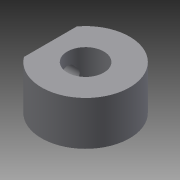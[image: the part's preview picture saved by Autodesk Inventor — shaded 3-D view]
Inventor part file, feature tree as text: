
AUTODESK INVENTOR PART (.ipt)
format: ipt  version: 2013 SP2 (Build 170200200, 200)  size: 86,016 bytes
history: native  units: in
note: dims shown in document units (in); Inventor stores cm internally (conversion verified against a paired STEP export)
features: extrude x2, sketch x2
ambient origin geometry x8: Origin, YZ Plane, XZ Plane, XY Plane, X Axis, Y Axis, Z Axis, Center Point
bodies: Solid1 (feature_tree)
feature tree (4):
  extrude  "Extrusion1"  Depth=0.415in
  extrude  "Extrusion2"  Depth=0.1in
  sketch  "Sketch1"  dims[d0=1.0in d1=0.415in]
  sketch  "Sketch2"  dims[d2=0.5in d3=0.0in d4=0.1in d5=0.2188in d6=0.5in d7=0.0in]
